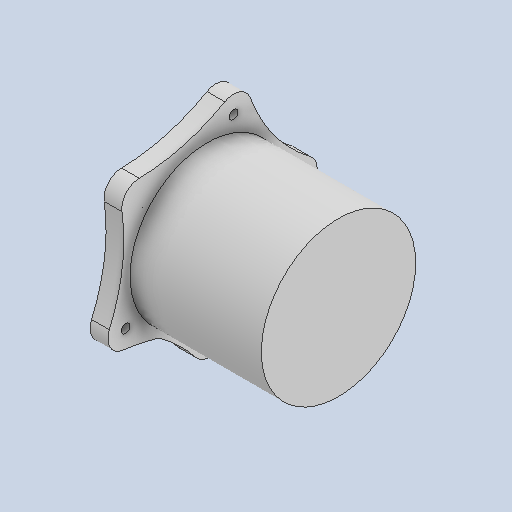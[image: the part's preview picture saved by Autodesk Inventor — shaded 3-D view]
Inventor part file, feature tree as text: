
AUTODESK INVENTOR PART (.ipt)
format: ipt  version: 2023 (Build 270158000, 158)  size: 324,608 bytes
history: native  units: mm
features: extrude x4, sketch x4, other x1, fillet x1
ambient origin geometry x8: Origin, YZ Plane, XZ Plane, XY Plane, X Axis, Y Axis, Z Axis, Center Point
bodies: Body1 (feature_tree)
feature tree (10):
  other  "Твердое тело1"
  extrude  "Выдавливание1"  Depth=10.0mm TaperAngle=0.0deg
  extrude  "Выдавливание2"  Depth=87.0mm
  extrude  "Выдавливание3"  Depth=74.0mm TaperAngle=0.0deg
  extrude  "Выдавливание4"  Depth=70.0mm
  fillet  "Сопряжение1"  Radius=5.0mm
  sketch  "Эскиз1"
  sketch  "Эскиз2"
  sketch  "Эскиз3"
  sketch  "Эскиз4"
